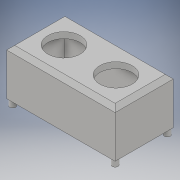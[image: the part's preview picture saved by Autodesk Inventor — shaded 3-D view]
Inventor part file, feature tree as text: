
AUTODESK INVENTOR PART (.ipt)
format: ipt  version: 2019 (Build 230136000, 136)  size: 365,568 bytes
history: native  units: mm
features: sketch x10, extrude x9, projected_geometry x9, chamfer x4
ambient origin geometry x8: Origin, YZ Plane, XZ Plane, XY Plane, X Axis, Y Axis, Z Axis, Center Point
bodies: Solid1 (feature_tree)
feature tree (32):
  extrude  "Extrusion1"  Depth=16.1mm
  extrude  "Extrusion11"  Depth=29.0mm
  extrude  "Extrusion12"  Depth=54.0mm
  chamfer  "Chamfer5"  Distance=3.0mm
  extrude  "Extrusion2"  Depth=48.0mm
  extrude  "Extrusion3"  Depth=51.0mm
  extrude  "Extrusion4"  Depth=3.0mm
  extrude  "Extrusion5"  Depth=3.0mm TaperAngle=0.0deg
  chamfer  "Chamfer1"  Distance=3.5mm
  chamfer  "Chamfer2"  Distance=4.0mm
  extrude  "Extrusion6"  Depth=3.0mm
  extrude  "Extrusion7"  Depth=3.0mm
  chamfer  "Chamfer3"  Distance=20.0mm
  sketch  "Sketch8"  dims[d13=25.0mm d14=0.0mm d15=51.0mm]
  sketch  "Sketch1"  dims[d0=16.1mm d1=16.1mm]
  sketch  "Sketch2"  dims[d2=25.9mm d3=29.0mm]
  sketch  "Sketch3"  dims[d4=54.0mm d5=14.5mm]
  sketch  "Sketch4"  dims[d6=14.5mm]
  sketch  "Sketch5"  dims[d7=14.05mm]
  projected_geometry  "Projected Loop1"
  projected_geometry  "Projected Loop2"
  projected_geometry  "Projected Loop3"
  projected_geometry  "Projected Loop4"
  sketch  "Sketch6"  dims[d8=14.05mm d9=3.0mm d10=0.0mm]
  projected_geometry  "Projected Loop5"
  projected_geometry  "Projected Loop6"
  sketch  "Sketch7"  dims[d11=23.0mm d12=48.0mm]
  projected_geometry  "Projected Loop7"
  projected_geometry  "Projected Loop8"
  sketch  "Sketch12"  dims[d16=3.0mm d17=0.0mm d18=45.0mm]
  projected_geometry  "Projected Loop12"
  sketch  "Sketch13"  dims[d19=48.0mm d20=15.0mm d21=0.0mm d22=3.5mm d23=4.0mm d24=4.0mm d25=4.0mm d26=20.0mm d28=40.0mm d29=20.0mm d31=37.0mm d34=10.0mm d35=0.0mm d36=2.0mm d37=2.0mm d38=45.0deg d39=2.0mm d40=2.0mm d41=45.0deg d42=6.0mm d43=20.0mm d45=40.0mm d46=20.0mm d48=37.0mm d51=10.0mm d52=0.0mm d53=4.0mm d54=15.0mm d55=3.0mm d56=18.0mm d57=18.0mm d58=16.0mm d59=0.0mm d60=2.0mm d61=2.0mm d62=45.0deg d63=6.0mm d85=3.0mm d86=3.0mm d87=3.0mm d88=3.0mm d89=20.0mm d90=0.0mm d91=1.5mm d92=1.5mm d93=2.9mm d94=20.0mm d96=51.0mm d97=20.0mm d99=26.0mm d102=3.0mm d103=0.0mm d104=2.0mm d105=2.0mm d106=45.0deg]
